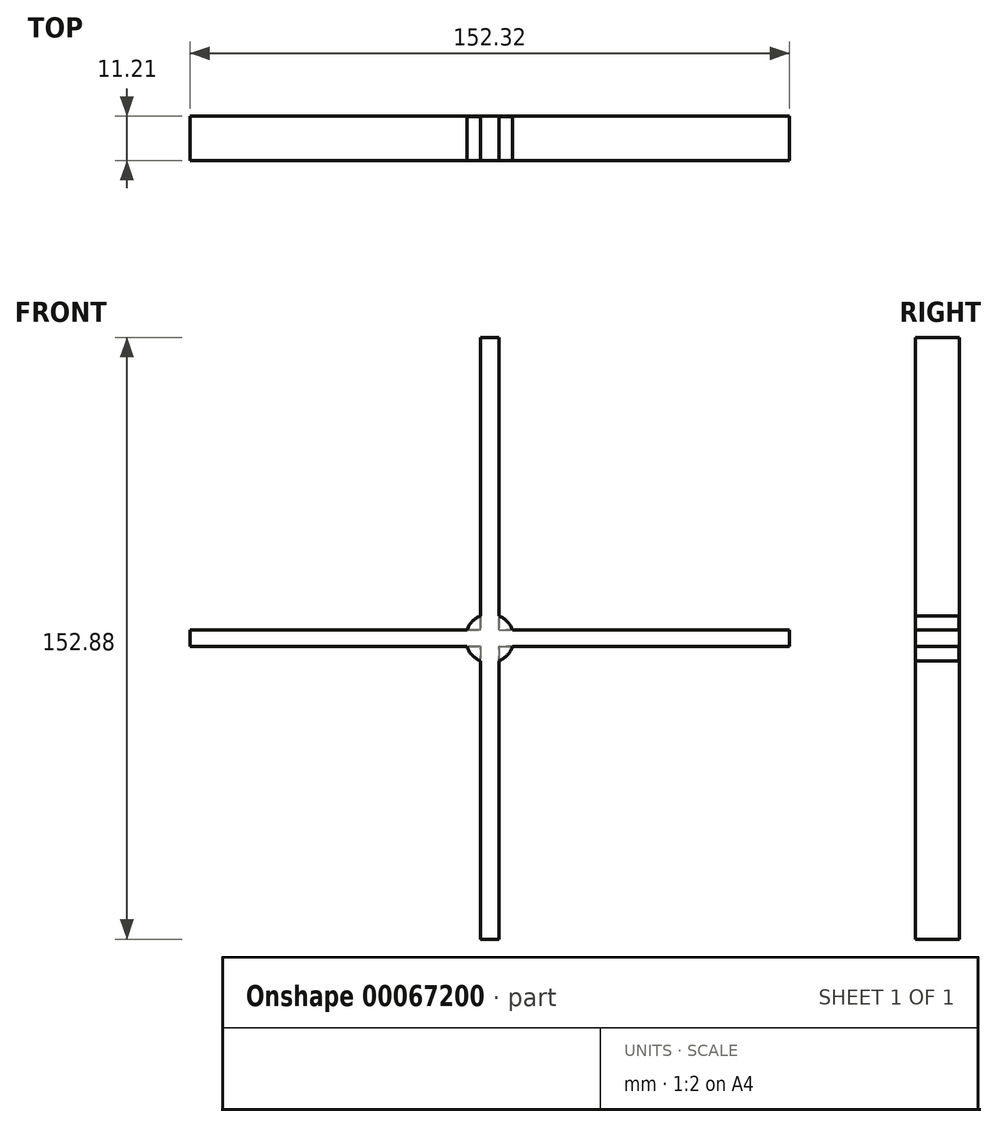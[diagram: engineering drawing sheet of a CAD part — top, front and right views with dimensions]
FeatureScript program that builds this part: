
annotation { "Feature Type Name" : "Feature", "Feature Type Description" : "" }
export const myFeature = defineFeature(function(context is Context, id is Id, definition is map)
    precondition{}
    {
        {
            var Q0;
            Q0=qCreatedBy(makeId("Front.planeOp"),FACE);
            var sketch = newSketch(context, id + "F0", { "sketchPlane" : qUnion([Q0])});
            skLineSegment(sketch, "E0.rect.bottom", {"start": v(2.34, -76.44) * mm, "end": v(-2.34, -76.44) * mm});
            skLineSegment(sketch, "E0.rect.top", {"start": v(2.34, 76.44) * mm, "end": v(-2.34, 76.44) * mm});
            skLineSegment(sketch, "E0.rect.left", {"start": v(2.34, -76.44) * mm, "end": v(2.34, 76.44) * mm});
            skLineSegment(sketch, "E0.rect.right", {"start": v(-2.34, -76.44) * mm, "end": v(-2.34, 76.44) * mm});
            skPoint(sketch, "E0.rect.middle", {"position": v(0, 0) * mm});
            skLineSegment(sketch, "E1.rect.bottom", {"start": v(76.16, -2.08) * mm, "end": v(-76.16, -2.08) * mm});
            skLineSegment(sketch, "E1.rect.top", {"start": v(76.16, 2.08) * mm, "end": v(-76.16, 2.08) * mm});
            skLineSegment(sketch, "E1.rect.left", {"start": v(76.16, -2.08) * mm, "end": v(76.16, 2.08) * mm});
            skLineSegment(sketch, "E1.rect.right", {"start": v(-76.16, -2.08) * mm, "end": v(-76.16, 2.08) * mm});
            skSolve(sketch);
        }
        {
            var Q0;
            Q0 = qSketchRegion(id + "F0", true);
            extrude(context, id + "F1", {"entities" : qUnion([Q0]), "oppositeDirection" : true, "depth" : 11.21 * mm});
        }
        {
            var Q0;
            Q0=qCreatedBy(makeId("Front.planeOp"),FACE);
            var sketch = newSketch(context, id + "F2", { "sketchPlane" : qUnion([Q0])});
            skCircle(sketch, "E2", {"center": v(0, 0) * mm, "radius": 6.17 * mm});
            skSolve(sketch);
        }
        {
            var Q0;
            Q0 = qSketchRegion(id + "F2", true);
            extrude(context, id + "F3", {"entities" : qUnion([Q0]), "operationType" : NewBodyOperationType.ADD, "oppositeDirection" : true, "depth" : 11.1 * mm});
        }
    });
